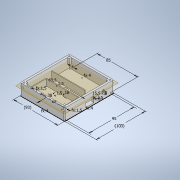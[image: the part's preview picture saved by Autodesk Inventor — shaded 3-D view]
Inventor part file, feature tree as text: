
AUTODESK INVENTOR PART (.ipt)
format: ipt  version: 2022 (Build 260153000, 153)  size: 293,888 bytes
history: native  units: mm
features: extrude x10, sketch x4, other x2, fillet x1
ambient origin geometry x8: Origin, YZ Plane, XZ Plane, XY Plane, X Axis, Y Axis, Z Axis, Center Point
bodies: Body1 (feature_tree)
feature tree (17):
  other  "Těleso1"
  sketch  "Náčrt1"
  extrude  "Vysunutí1"  Depth=4.0mm
  extrude  "Vysunutí2"  Depth=4.0mm
  sketch  "Náčrt2"
  extrude  "Vysunutí5"  Depth=4.0mm
  extrude  "Vysunutí6"  Depth=4.0mm
  other  "Pracovní rovina1"
  extrude  "Vysunutí7"  Depth=85.0mm
  extrude  "Vysunutí8"  Depth=95.0mm
  extrude  "Vysunutí9"  Depth=1.5mm
  fillet  "Zaoblení1"  Radius=69.5mm
  extrude  "Vysunutí10"  Depth=2.5mm
  extrude  "Vysunutí11"  Depth=2.5mm
  extrude  "Vysunutí12"  Depth=15.5mm
  sketch  "Náčrt3"
  sketch  "Náčrt4"
